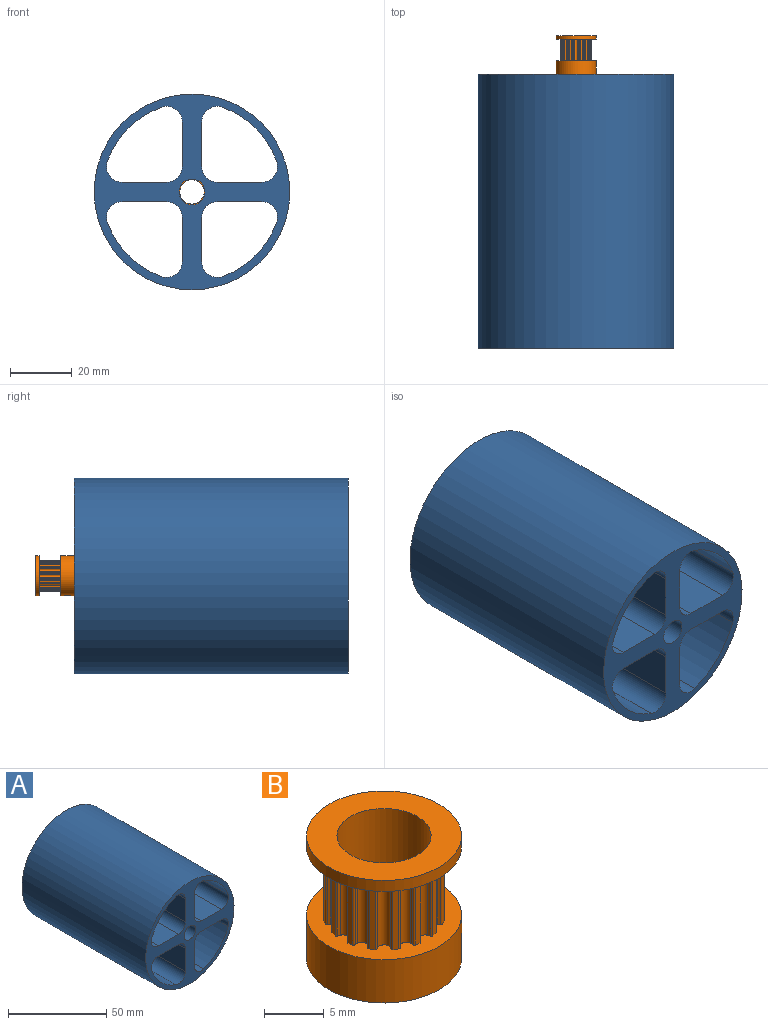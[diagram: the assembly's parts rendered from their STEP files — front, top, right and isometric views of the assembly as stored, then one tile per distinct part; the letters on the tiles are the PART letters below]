
ASSEMBLY  parts=2 mates=1
PART A: 28 faces, bbox 63.5x88.9x63.5 mm
  f0: cylinder r=29.21mm len=88.9mm, axis (0,1,0), area 2265.6mm2, adj f14,f15,f25,f27
  f1: plane 88.9x14.42mm, normal (-1,0,0), area 1281.9mm2, adj f14,f15,f25,f26
  f2: cylinder r=29.21mm len=88.9mm, axis (0,1,0), area 2265.6mm2, adj f14,f15,f22,f24
  f3: plane 88.9x14.42mm, normal (1,0,0), area 1281.9mm2, adj f14,f15,f22,f23
  f4: plane 88.9x14.42mm, normal (0,0,-1), area 1281.9mm2, adj f14,f15,f19,f21
  f5: plane 88.9x14.42mm, normal (-1,0,0), area 1281.9mm2, adj f14,f15,f19,f20
  f6: plane 88.9x14.42mm, normal (1,0,0), area 1281.9mm2, adj f14,f15,f16,f18
  f7: cylinder r=29.21mm len=88.9mm, axis (0,1,0), area 2265.6mm2, adj f14,f15,f16,f17
  f8: plane 88.9x14.42mm, normal (0,0,-1), area 1281.9mm2, adj f14,f15,f23,f24
  f9: cylinder r=31.75mm len=88.9mm, axis (0,1,0), area 17734.8mm2, adj f14,f15
  f10: cylinder r=4.19mm len=88.9mm, axis (0,1,0), area 2341mm2, adj f14,f15
  f11: cylinder r=29.21mm len=88.9mm, axis (0,1,0), area 2265.6mm2, adj f14,f15,f20,f21
  f12: plane 88.9x14.42mm, normal (0,0,1), area 1281.9mm2, adj f14,f15,f17,f18
  f13: plane 88.9x14.42mm, normal (0,0,1), area 1281.9mm2, adj f14,f15,f26,f27
  f14: plane 63.5x63.5mm, normal (0,-1,0), area 1233.8mm2, adj f0,f1,f2,f3,f4,f5,f6,f7
  f15: plane 63.5x63.5mm, normal (0,1,0), area 1233.8mm2, adj f0,f1,f2,f3,f4,f5,f6,f7
  f16: cylinder r=5.08mm len=88.9mm, axis (0,1,0), area 867.1mm2, adj f6,f7,f14,f15
  f17: cylinder r=5.08mm len=88.9mm, axis (0,1,0), area 867.1mm2, adj f7,f12,f14,f15
  f18: cylinder r=5.08mm len=88.9mm, axis (0,-1,0), area 709.4mm2, adj f6,f12,f14,f15
  f19: cylinder r=5.08mm len=88.9mm, axis (0,-1,0), area 709.4mm2, adj f4,f5,f14,f15
  f20: cylinder r=5.08mm len=88.9mm, axis (0,1,0), area 867.1mm2, adj f5,f11,f14,f15
  f21: cylinder r=5.08mm len=88.9mm, axis (0,1,0), area 867.1mm2, adj f4,f11,f14,f15
  f22: cylinder r=5.08mm len=88.9mm, axis (0,1,0), area 867.1mm2, adj f2,f3,f14,f15
  f23: cylinder r=5.08mm len=88.9mm, axis (0,-1,0), area 709.4mm2, adj f3,f8,f14,f15
  f24: cylinder r=5.08mm len=88.9mm, axis (0,1,0), area 867.1mm2, adj f2,f8,f14,f15
  f25: cylinder r=5.08mm len=88.9mm, axis (0,1,0), area 867.1mm2, adj f0,f1,f14,f15
  f26: cylinder r=5.08mm len=88.9mm, axis (0,-1,0), area 709.4mm2, adj f1,f13,f14,f15
  f27: cylinder r=5.08mm len=88.9mm, axis (0,1,0), area 867.1mm2, adj f0,f13,f14,f15
PART B: 104 faces, bbox 13x13x12.6 mm
  f0: cylinder r=3.94mm len=12.58mm, axis (0,0,1), area 304.5mm2, adj f2,f102,f103
  f1: cylinder r=6.5mm len=13mm, axis (0,0,1), area 174.4mm2, adj f2,f3,f103
  f2: plane 13x13mm, normal (0,0,-1), area 83.8mm2, adj f0,f1
  f3: plane 13x13mm, normal (0,0,1), area 62.7mm2, adj f1,f4,f5,f6,f7,f8,f9,f10
  f4: cylinder r=0.15mm len=7mm, axis (0,0,-1), area 1.7mm2, adj f3,f5,f99,f100
  f5: cylinder r=1mm len=7mm, axis (0,0,-1), area 1.7mm2, adj f3,f4,f6,f100
  f6: cylinder r=0.56mm len=7mm, axis (0,0,-1), area 9mm2, adj f3,f5,f7,f100
  f7: cylinder r=1mm len=7mm, axis (0,0,-1), area 1.7mm2, adj f3,f6,f8,f100
  f8: cylinder r=0.15mm len=7mm, axis (0,0,-1), area 1.7mm2, adj f3,f7,f9,f100
  f9: plane 7x0.49mm, normal (0.98,0.2,0), area 3.5mm2, adj f3,f8,f10,f100
  f10: cylinder r=0.15mm len=7mm, axis (0,0,-1), area 1.7mm2, adj f3,f9,f11,f100
  f11: cylinder r=1mm len=7mm, axis (0,0,-1), area 1.7mm2, adj f3,f10,f12,f100
  f12: cylinder r=0.56mm len=7mm, axis (0,0,-1), area 9mm2, adj f3,f11,f13,f100
  f13: cylinder r=1mm len=7mm, axis (0,0,-1), area 1.7mm2, adj f3,f12,f14,f100
  f14: cylinder r=0.15mm len=7mm, axis (0,0,-1), area 1.7mm2, adj f3,f13,f15,f100
  f15: plane 7x0.41mm, normal (0.83,0.56,0), area 3.5mm2, adj f3,f14,f16,f100
  f16: cylinder r=0.15mm len=7mm, axis (0,0,-1), area 1.7mm2, adj f3,f15,f17,f100
  f17: cylinder r=1mm len=7mm, axis (0,0,-1), area 1.7mm2, adj f3,f16,f18,f100
  f18: cylinder r=0.56mm len=7mm, axis (0,0,-1), area 9mm2, adj f3,f17,f19,f100
  f19: cylinder r=1mm len=7mm, axis (0,0,-1), area 1.7mm2, adj f3,f18,f20,f100
  f20: cylinder r=0.15mm len=7mm, axis (0,0,-1), area 1.7mm2, adj f3,f19,f21,f100
  f21: plane 7x0.41mm, normal (0.56,0.83,0), area 3.5mm2, adj f3,f20,f22,f100
  f22: cylinder r=0.15mm len=7mm, axis (0,0,-1), area 1.7mm2, adj f3,f21,f23,f100
  f23: cylinder r=1mm len=7mm, axis (0,0,-1), area 1.7mm2, adj f3,f22,f24,f100
  f24: cylinder r=0.56mm len=7mm, axis (0,0,-1), area 9mm2, adj f3,f23,f25,f100
  f25: cylinder r=1mm len=7mm, axis (0,0,-1), area 1.7mm2, adj f3,f24,f26,f100
  f26: cylinder r=0.15mm len=7mm, axis (0,0,-1), area 1.7mm2, adj f3,f25,f27,f100
  f27: plane 7x0.49mm, normal (0.2,0.98,0), area 3.5mm2, adj f3,f26,f28,f100
  f28: cylinder r=0.15mm len=7mm, axis (0,0,-1), area 1.7mm2, adj f3,f27,f29,f100
  f29: cylinder r=1mm len=7mm, axis (0,0,-1), area 1.7mm2, adj f3,f28,f30,f100
  f30: cylinder r=0.56mm len=7mm, axis (0,0,-1), area 9mm2, adj f3,f29,f31,f100
  f31: cylinder r=1mm len=7mm, axis (0,0,-1), area 1.7mm2, adj f3,f30,f32,f100
  f32: cylinder r=0.15mm len=7mm, axis (0,0,-1), area 1.7mm2, adj f3,f31,f33,f100
  f33: plane 7x0.49mm, normal (-0.2,0.98,0), area 3.5mm2, adj f3,f32,f34,f100
  f34: cylinder r=0.15mm len=7mm, axis (0,0,-1), area 1.7mm2, adj f3,f33,f35,f100
  f35: cylinder r=1mm len=7mm, axis (0,0,-1), area 1.7mm2, adj f3,f34,f36,f100
  f36: cylinder r=0.56mm len=7mm, axis (0,0,-1), area 9mm2, adj f3,f35,f37,f100
  f37: cylinder r=1mm len=7mm, axis (0,0,-1), area 1.7mm2, adj f3,f36,f38,f100
  f38: cylinder r=0.15mm len=7mm, axis (0,0,-1), area 1.7mm2, adj f3,f37,f39,f100
  f39: plane 7x0.41mm, normal (-0.56,0.83,0), area 3.5mm2, adj f3,f38,f40,f100
  f40: cylinder r=0.15mm len=7mm, axis (0,0,-1), area 1.7mm2, adj f3,f39,f41,f100
  f41: cylinder r=1mm len=7mm, axis (0,0,-1), area 1.7mm2, adj f3,f40,f42,f100
  f42: cylinder r=0.56mm len=7mm, axis (0,0,-1), area 9mm2, adj f3,f41,f43,f100
  f43: cylinder r=1mm len=7mm, axis (0,0,-1), area 1.7mm2, adj f3,f42,f44,f100
  f44: cylinder r=0.15mm len=7mm, axis (0,0,-1), area 1.7mm2, adj f3,f43,f45,f100
  f45: plane 7x0.41mm, normal (-0.83,0.56,0), area 3.5mm2, adj f3,f44,f46,f100
  f46: cylinder r=0.15mm len=7mm, axis (0,0,-1), area 1.7mm2, adj f3,f45,f47,f100
  f47: cylinder r=1mm len=7mm, axis (0,0,-1), area 1.7mm2, adj f3,f46,f48,f100
  f48: cylinder r=0.56mm len=7mm, axis (0,0,-1), area 9mm2, adj f3,f47,f49,f100
  f49: cylinder r=1mm len=7mm, axis (0,0,-1), area 1.7mm2, adj f3,f48,f50,f100
  f50: cylinder r=0.15mm len=7mm, axis (0,0,-1), area 1.7mm2, adj f3,f49,f51,f100
  f51: plane 7x0.49mm, normal (-0.98,0.2,0), area 3.5mm2, adj f3,f50,f52,f100
  f52: cylinder r=0.15mm len=7mm, axis (0,0,-1), area 1.7mm2, adj f3,f51,f53,f100
  f53: cylinder r=1mm len=7mm, axis (0,0,-1), area 1.7mm2, adj f3,f52,f54,f100
  f54: cylinder r=0.56mm len=7mm, axis (0,0,-1), area 9mm2, adj f3,f53,f55,f100
  f55: cylinder r=1mm len=7mm, axis (0,0,-1), area 1.7mm2, adj f3,f54,f56,f100
  f56: cylinder r=0.15mm len=7mm, axis (0,0,-1), area 1.7mm2, adj f3,f55,f57,f100
  f57: plane 7x0.49mm, normal (-0.98,-0.2,0), area 3.5mm2, adj f3,f56,f58,f100
  f58: cylinder r=0.15mm len=7mm, axis (0,0,-1), area 1.7mm2, adj f3,f57,f59,f100
  f59: cylinder r=1mm len=7mm, axis (0,0,-1), area 1.7mm2, adj f3,f58,f60,f100
  f60: cylinder r=0.56mm len=7mm, axis (0,0,-1), area 9mm2, adj f3,f59,f61,f100
  f61: cylinder r=1mm len=7mm, axis (0,0,-1), area 1.7mm2, adj f3,f60,f62,f100
  f62: cylinder r=0.15mm len=7mm, axis (0,0,-1), area 1.7mm2, adj f3,f61,f63,f100
  f63: plane 7x0.41mm, normal (-0.83,-0.56,0), area 3.5mm2, adj f3,f62,f64,f100
  f64: cylinder r=0.15mm len=7mm, axis (0,0,-1), area 1.7mm2, adj f3,f63,f65,f100
  f65: cylinder r=1mm len=7mm, axis (0,0,-1), area 1.7mm2, adj f3,f64,f66,f100
  f66: cylinder r=0.56mm len=7mm, axis (0,0,-1), area 9mm2, adj f3,f65,f67,f100
  f67: cylinder r=1mm len=7mm, axis (0,0,-1), area 1.7mm2, adj f3,f66,f68,f100
  f68: cylinder r=0.15mm len=7mm, axis (0,0,-1), area 1.7mm2, adj f3,f67,f69,f100
  f69: plane 7x0.41mm, normal (-0.56,-0.83,0), area 3.5mm2, adj f3,f68,f70,f100
  f70: cylinder r=0.15mm len=7mm, axis (0,0,-1), area 1.7mm2, adj f3,f69,f71,f100
  f71: cylinder r=1mm len=7mm, axis (0,0,-1), area 1.7mm2, adj f3,f70,f72,f100
  f72: cylinder r=0.56mm len=7mm, axis (0,0,-1), area 9mm2, adj f3,f71,f73,f100
  f73: cylinder r=1mm len=7mm, axis (0,0,-1), area 1.7mm2, adj f3,f72,f74,f100
  f74: cylinder r=0.15mm len=7mm, axis (0,0,-1), area 1.7mm2, adj f3,f73,f75,f100
  f75: plane 7x0.49mm, normal (-0.2,-0.98,0), area 3.5mm2, adj f3,f74,f76,f100
  f76: cylinder r=0.15mm len=7mm, axis (0,0,-1), area 1.7mm2, adj f3,f75,f77,f100
  f77: cylinder r=1mm len=7mm, axis (0,0,-1), area 1.7mm2, adj f3,f76,f78,f100
  f78: cylinder r=0.56mm len=7mm, axis (0,0,-1), area 9mm2, adj f3,f77,f79,f100
  f79: cylinder r=1mm len=7mm, axis (0,0,-1), area 1.7mm2, adj f3,f78,f80,f100
  f80: cylinder r=0.15mm len=7mm, axis (0,0,-1), area 1.7mm2, adj f3,f79,f81,f100
  f81: plane 7x0.49mm, normal (0.2,-0.98,0), area 3.5mm2, adj f3,f80,f82,f100
  f82: cylinder r=0.15mm len=7mm, axis (0,0,-1), area 1.7mm2, adj f3,f81,f83,f100
  f83: cylinder r=1mm len=7mm, axis (0,0,-1), area 1.7mm2, adj f3,f82,f84,f100
  f84: cylinder r=0.56mm len=7mm, axis (0,0,-1), area 9mm2, adj f3,f83,f85,f100
  f85: cylinder r=1mm len=7mm, axis (0,0,-1), area 1.7mm2, adj f3,f84,f86,f100
  f86: cylinder r=0.15mm len=7mm, axis (0,0,-1), area 1.7mm2, adj f3,f85,f87,f100
  f87: plane 7x0.41mm, normal (0.56,-0.83,0), area 3.5mm2, adj f3,f86,f88,f100
  f88: cylinder r=0.15mm len=7mm, axis (0,0,-1), area 1.7mm2, adj f3,f87,f89,f100
  f89: cylinder r=1mm len=7mm, axis (0,0,-1), area 1.7mm2, adj f3,f88,f90,f100
  f90: cylinder r=0.56mm len=7mm, axis (0,0,-1), area 9mm2, adj f3,f89,f91,f100
  f91: cylinder r=1mm len=7mm, axis (0,0,-1), area 1.7mm2, adj f3,f90,f92,f100
  f92: cylinder r=0.15mm len=7mm, axis (0,0,-1), area 1.7mm2, adj f3,f91,f93,f100
  f93: plane 7x0.41mm, normal (0.83,-0.56,0), area 3.5mm2, adj f3,f92,f94,f100
  f94: cylinder r=0.15mm len=7mm, axis (0,0,-1), area 1.7mm2, adj f3,f93,f95,f100
  f95: cylinder r=1mm len=7mm, axis (0,0,-1), area 1.7mm2, adj f3,f94,f96,f100
  f96: cylinder r=0.56mm len=7mm, axis (0,0,-1), area 9mm2, adj f3,f95,f97,f100
  f97: cylinder r=1mm len=7mm, axis (0,0,-1), area 1.7mm2, adj f3,f96,f98,f100
  f98: cylinder r=0.15mm len=7mm, axis (0,0,-1), area 1.7mm2, adj f3,f97,f99,f100
  f99: plane 7x0.49mm, normal (0.98,-0.2,0), area 3.5mm2, adj f3,f4,f98,f100
  f100: plane 13x13mm, normal (0,0,-1), area 62.7mm2, adj f4,f5,f6,f7,f8,f9,f10,f11
  f101: cylinder r=6.5mm len=13mm, axis (0,0,-1), area 46.1mm2, adj f100,f102
  f102: plane 13x13mm, normal (0,0,1), area 83.8mm2, adj f0,f101
  f103: cylinder r=1.5mm len=3mm, axis (0,-1,0), area 24.6mm2, adj f0,f1
PLACE A t=(-22.52,-40.11,-39.17)mm
PLACE B rot(axis=(-1,0,0),90deg) t=(-22.52,-35.67,-39.17)mm
MATE fastened B.f0 <-> A.f10  axis (0,1,0) through (-22.52,-40.11,-39.17)mm
